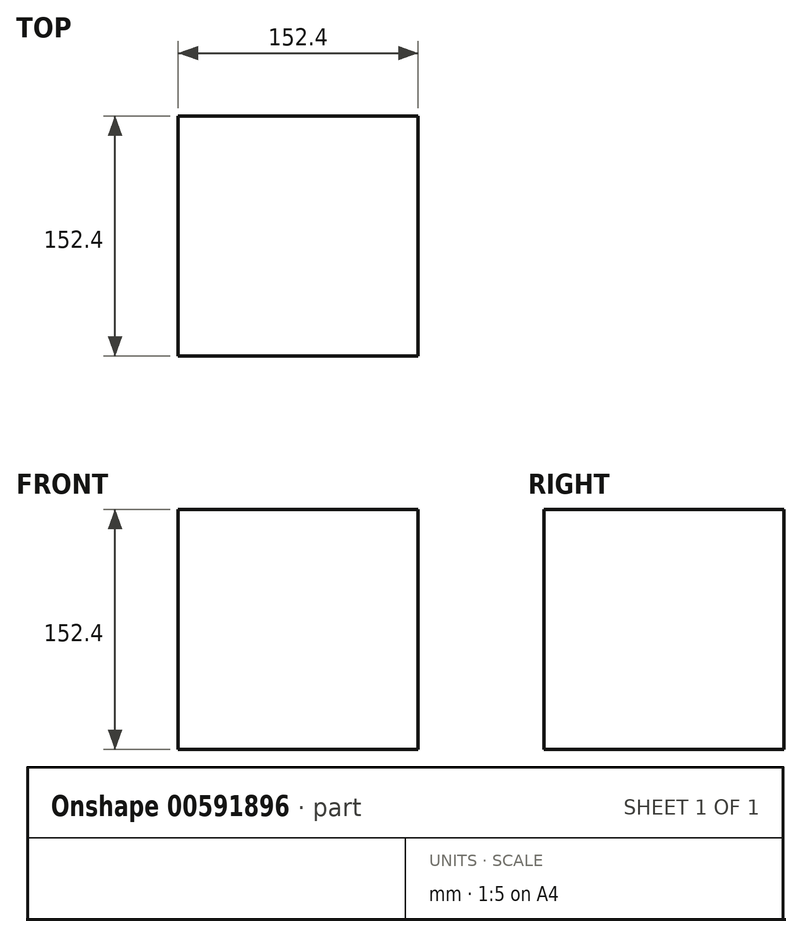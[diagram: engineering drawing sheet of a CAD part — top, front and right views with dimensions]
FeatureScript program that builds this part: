
annotation { "Feature Type Name" : "Feature", "Feature Type Description" : "" }
export const myFeature = defineFeature(function(context is Context, id is Id, definition is map)
    precondition{}
    {
        {
            var Q0;
            Q0=qCreatedBy(makeId("Top.planeOp"),FACE);
            var sketch = newSketch(context, id + "F0", { "sketchPlane" : qUnion([Q0])});
            skLineSegment(sketch, "E0.bottom", {"start": v(76.2, 76.2) * mm, "end": v(-76.2, 76.2) * mm});
            skLineSegment(sketch, "E0.top", {"start": v(76.2, -76.2) * mm, "end": v(-76.2, -76.2) * mm});
            skLineSegment(sketch, "E0.left", {"start": v(76.2, 76.2) * mm, "end": v(76.2, -76.2) * mm});
            skLineSegment(sketch, "E0.right", {"start": v(-76.2, 76.2) * mm, "end": v(-76.2, -76.2) * mm});
            skPoint(sketch, "E0.middle", {"position": v(0, 0) * mm});
            skSolve(sketch);
        }
        {
            var Q0;
            Q0 = qSketchRegion(id + "F0", true);
            extrude(context, id + "F1", {"entities" : qUnion([Q0]), "depth" : 152.4 * mm, "offsetDistance" : 25 * mm, "symmetric" : true});
        }
    });
